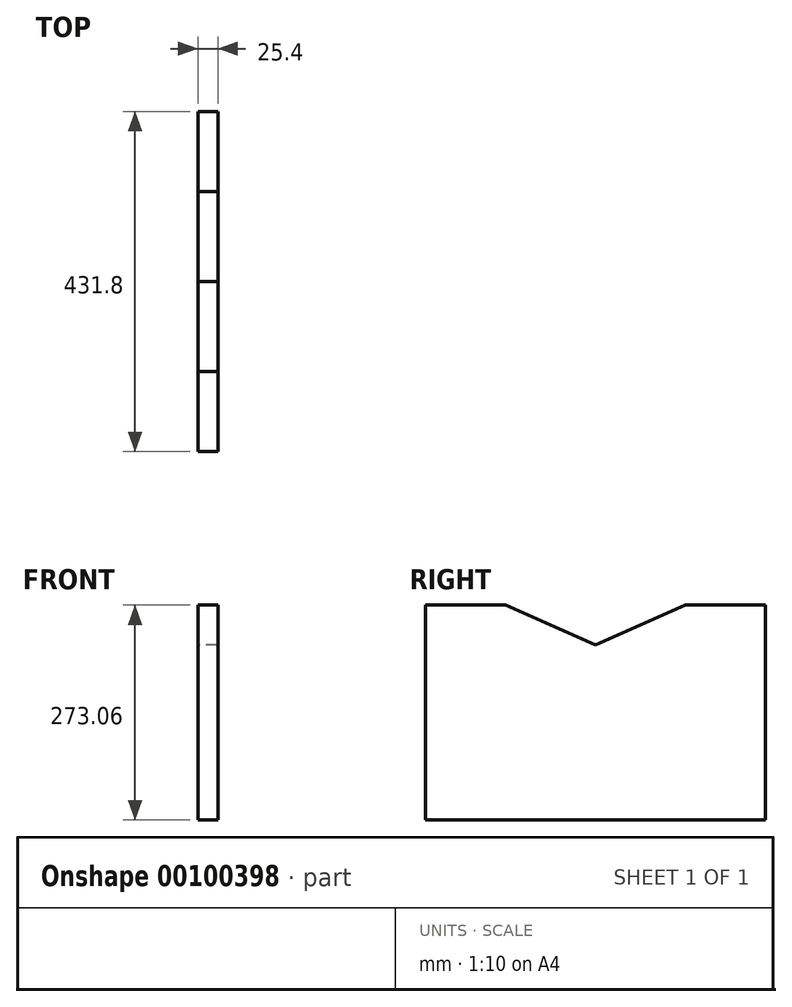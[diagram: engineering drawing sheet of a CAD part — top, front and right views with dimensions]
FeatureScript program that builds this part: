
annotation { "Feature Type Name" : "Feature", "Feature Type Description" : "" }
export const myFeature = defineFeature(function(context is Context, id is Id, definition is map)
    precondition{}
    {
        {
            var Q0;
            Q0=qCreatedBy(makeId("Right.planeOp"),FACE);
            var sketch = newSketch(context, id + "F0", { "sketchPlane" : qUnion([Q0])});
            skLineSegment(sketch, "E0.bottom", {"start": v(-215.9, 136.53) * mm, "end": v(-114.3, 136.53) * mm});
            skLineSegment(sketch, "E0.top", {"start": v(-215.9, -136.53) * mm, "end": v(215.9, -136.53) * mm});
            skLineSegment(sketch, "E0.left", {"start": v(-215.9, 136.53) * mm, "end": v(-215.9, -136.53) * mm});
            skLineSegment(sketch, "E0.right", {"start": v(215.9, 136.53) * mm, "end": v(215.9, -136.53) * mm});
            skPoint(sketch, "E0.middle", {"position": v(0, 0) * mm});
            skLineSegment(sketch, "E1", {"start": v(0, 136.53) * mm, "end": v(0, 85.72) * mm, "construction": true});
            skPoint(sketch, "E1.endSnap0", {"position": v(0, 136.53) * mm});
            skLineSegment(sketch, "E2.0", {"start": v(-114.3, 136.52) * mm, "end": v(-114.3, 85.72) * mm, "construction": true});
            skLineSegment(sketch, "E3", {"start": v(-114.3, 136.52) * mm, "end": v(0, 85.72) * mm});
            skLineSegment(sketch, "E4.MirrorCS", {"start": v(114.3, 136.53) * mm, "end": v(0, 85.72) * mm});
            skLineSegment(sketch, "E5.trimOffspring", {"start": v(114.3, 136.53) * mm, "end": v(215.9, 136.53) * mm});
            skSolve(sketch);
        }
        {
            var Q0;
            Q0 = qSketchRegion(id + "F0", true);
            extrude(context, id + "F1", {"entities" : qUnion([Q0]), "endBound" : BoundingType.SYMMETRIC, "depth" : 25.4 * mm});
        }
    });
